SOLIDWORKS PART (.sldprt)
format: sldprt  version: not decoded by parser v0  size: 130,560 bytes
history: native  units: mm
features: sketch x4, plane x3, extrude x3, fillet x2, material x1, shell x1, cut_extrude x1 + 1 further entry (+8 scaffold rows collapsed)
feature tree (24):
  scaffold x8  (default folders/planes/origin — collapsed)
  material  "Matériau <non spécifié>"
  "Corps de surface"
  plane  "Face"
  plane  "Dessus"
  plane  "Droite"
  sketch  "Esquisse1"  dims[D1=~26.906311mm]
  extrude  "Base-Extrusion"  Depth=19.6mm
  sketch  "Esquisse2"  dims[D1=~5.575533mm]
  extrude  "Boss.-Extru.1"  Depth=3.9mm
  sketch  "Esquisse3"  dims[D1=~1.81491mm]
  extrude  "Boss.-Extru.2"  Depth=1.35mm
  fillet  "Congé2"  Radius=0.5mm
  fillet  "Congé3"  Radius=0.5mm
  shell  "Coque1"  Thickness=0.3mm
  sketch  "Esquisse4"  dims[D1=~0.574147mm]
  cut_extrude  "Enlèv. mat.-Extru.1"  [1 undecoded]
decode coverage: 10 of 11 modeling features carry decoded parameters; 1 rows unclassified (native names shown)
note: ~ marks probable driven/reference dimensions
note: 1 parameter value undecoded
note: suppression state not decoded; provenance and decode notes live in map.json
